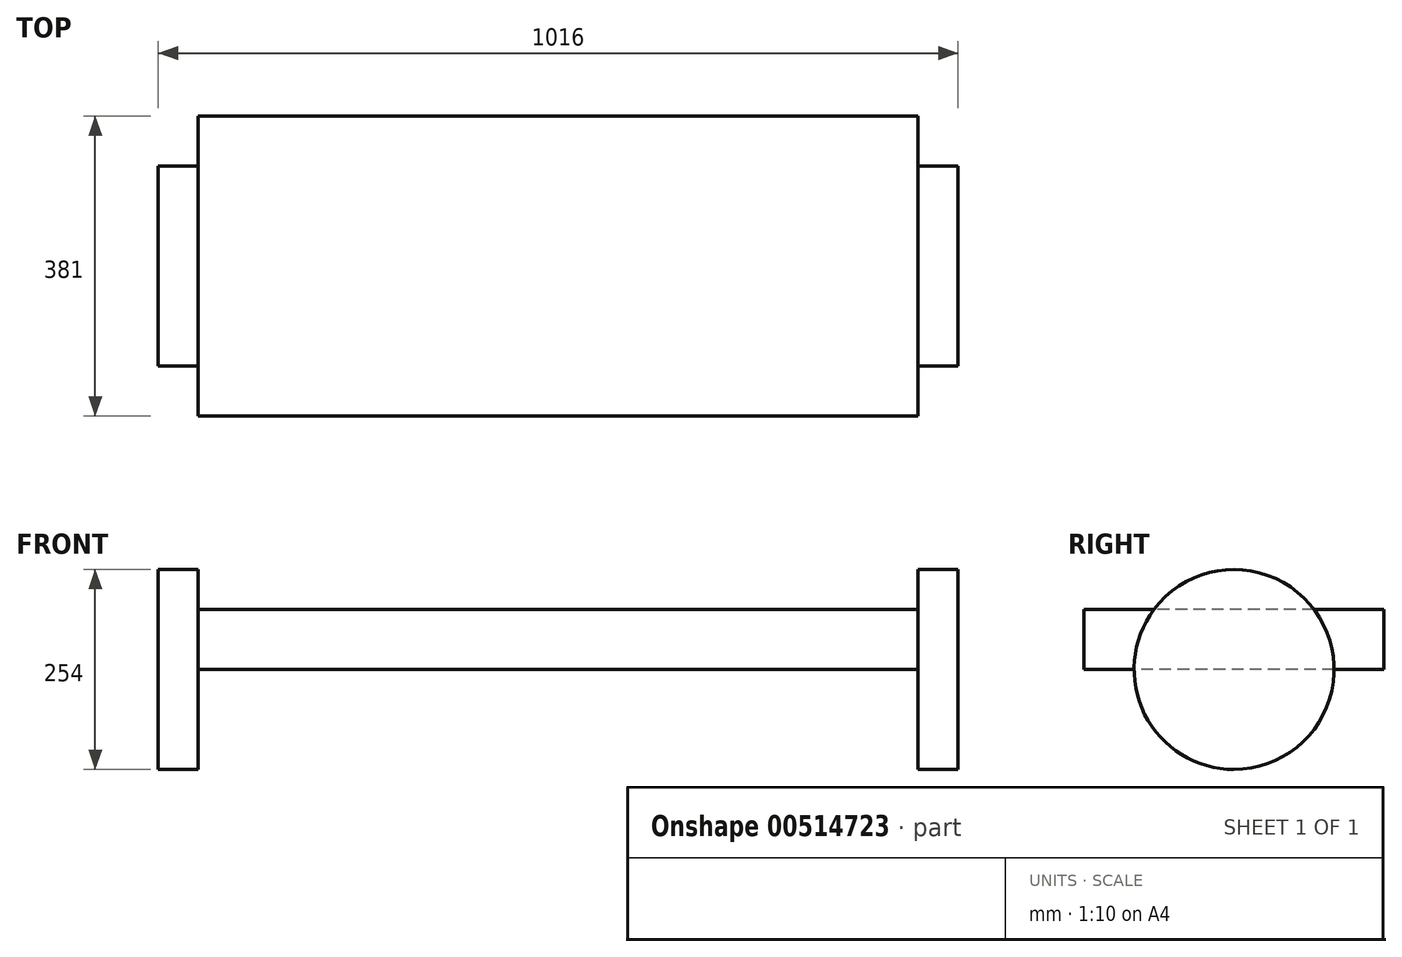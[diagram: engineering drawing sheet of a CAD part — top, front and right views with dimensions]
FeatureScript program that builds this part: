
annotation { "Feature Type Name" : "Feature", "Feature Type Description" : "" }
export const myFeature = defineFeature(function(context is Context, id is Id, definition is map)
    precondition{}
    {
        {
            var Q0;
            Q0=qCreatedBy(makeId("Top.planeOp"),FACE);
            var sketch = newSketch(context, id + "F0", { "sketchPlane" : qUnion([Q0])});
            skLineSegment(sketch, "E0.bottom", {"start": v(-244.84, 305.38) * mm, "end": v(669.56, 305.38) * mm});
            skLineSegment(sketch, "E0.top", {"start": v(-244.84, -75.62) * mm, "end": v(669.56, -75.62) * mm});
            skLineSegment(sketch, "E0.left", {"start": v(-244.84, 305.38) * mm, "end": v(-244.84, -75.62) * mm});
            skLineSegment(sketch, "E0.right", {"start": v(669.56, 305.38) * mm, "end": v(669.56, -75.62) * mm});
            skSolve(sketch);
        }
        {
            var Q0;
            Q0 = qSketchRegion(id + "F0", true);
            extrude(context, id + "F1", {"entities" : qUnion([Q0]), "depth" : 76.2 * mm, "offsetDistance" : 25.4 * mm});
        }
        {
            var Q0;
            Q0=makeQuery(id+"F1.opExtrude","SWEPT_FACE",FACE,{"disambiguationData":[OSD([sQuery(id+"F0.wireOp",EDGE,"E0.right")])]});
            var sketch = newSketch(context, id + "F2", { "sketchPlane" : qUnion([Q0])});
            skCircle(sketch, "E1", {"center": v(114.88, 0) * mm, "radius": 127 * mm});
            skSolve(sketch);
        }
        {
            var Q0;
            Q0 = qSketchRegion(id + "F2", true);
            extrude(context, id + "F3", {"entities" : qUnion([Q0]), "operationType" : NewBodyOperationType.ADD, "depth" : 50.8 * mm, "offsetDistance" : 25.4 * mm});
        }
        {
            var Q0;
            Q0=makeQuery(id+"F1.opExtrude","SWEPT_FACE",FACE,{"disambiguationData":[OSD([sQuery(id+"F0.wireOp",EDGE,"E0.left")])]});
            var sketch = newSketch(context, id + "F4", { "sketchPlane" : qUnion([Q0])});
            skCircle(sketch, "E2", {"center": v(-114.88, 0) * mm, "radius": 127 * mm});
            skSolve(sketch);
        }
        {
            var Q0;
            Q0 = qSketchRegion(id + "F4", true);
            extrude(context, id + "F5", {"entities" : qUnion([Q0]), "operationType" : NewBodyOperationType.ADD, "depth" : 50.8 * mm, "offsetDistance" : 25.4 * mm});
        }
    });
